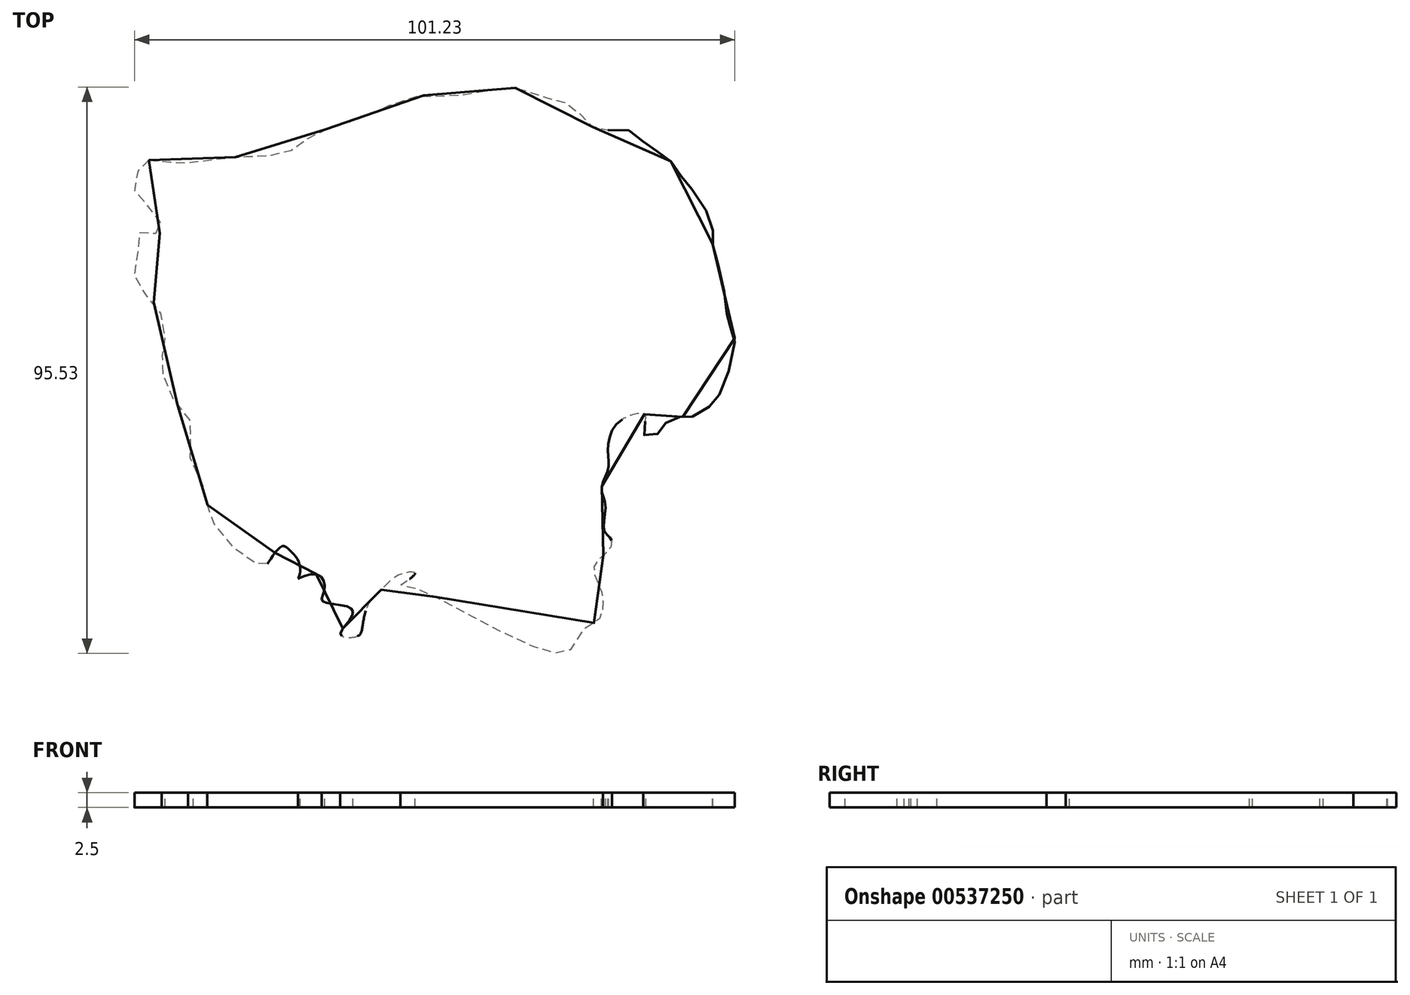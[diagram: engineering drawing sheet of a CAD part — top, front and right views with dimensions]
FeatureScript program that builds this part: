
annotation { "Feature Type Name" : "Feature", "Feature Type Description" : "" }
export const myFeature = defineFeature(function(context is Context, id is Id, definition is map)
    precondition{}
    {
        {
            var Q0;
            Q0=qCreatedBy(makeId("Top.planeOp"),FACE);
            var sketch = newSketch(context, id + "F0", { "sketchPlane" : qUnion([Q0])});
            skFitSpline(sketch, "E0", {"points": [v(-51.17, 29.84) * mm, v(-46.75, 29.42) * mm, v(-44.33, 29.42) * mm, v(-41.03, 29.86) * mm, v(-36.85, 30.3) * mm, v(-33.11, 30.52) * mm, v(-27.83, 31.17) * mm, v(-24.53, 33.38) * mm, v(-19.91, 35.58) * mm, v(-16.17, 36.68) * mm, v(-12.43, 38.22) * mm, v(-5.83, 40.64) * mm, v(0, 40.64) * mm, v(4.07, 41.3) * mm, v(8.9, 41.96) * mm, v(10.02, 42.18) * mm, v(15.73, 40.42) * mm, v(19.03, 39.54) * mm, v(21.9, 37.34) * mm, v(23.21, 35.8) * mm, v(25.41, 34.91) * mm, v(30.25, 34.7) * mm, v(32.9, 32.28) * mm, v(35.98, 30.52) * mm, v(38.4, 27.44) * mm, v(40.38, 25.01) * mm, v(43.9, 18.86) * mm, v(43.9, 16.21) * mm, v(45, 11.81) * mm, v(46.31, 4.34) * mm, v(46.53, 2.57) * mm, v(47.64, 0) * mm, v(45.44, -8.87) * mm, v(43.68, -11.5) * mm, v(40.16, -13.49) * mm, v(38.4, -13.48) * mm, v(35.97, -14.58) * mm, v(34.66, -16.35) * mm, v(32.45, -16.57) * mm, v(32.45, -14.59) * mm, v(32.46, -13.04) * mm, v(28.05, -14.36) * mm, v(26.3, -19.2) * mm, v(26.3, -22.29) * mm, v(25.2, -25.59) * mm, v(25.85, -28.45) * mm, v(25.63, -32.63) * mm, v(26.74, -33.95) * mm, v(26.74, -35.5) * mm, v(24.75, -37.47) * mm, v(23.87, -39.45) * mm, v(24.97, -42.3) * mm, v(25.42, -44.95) * mm, v(24.76, -47.6) * mm, v(21.9, -49.57) * mm, v(18.6, -53.31) * mm, v(-7.14, -42.09) * mm, v(-8.7, -41.87) * mm, v(-6.26, -39.89) * mm, v(-8.91, -40.1) * mm, v(-12.1, -42.75) * mm, v(-13.97, -44.73) * mm, v(-15.07, -48.47) * mm, v(-15.95, -50.46) * mm, v(-18.82, -50.23) * mm, v(-17.05, -47.37) * mm, v(-17.27, -45.61) * mm, v(-21.9, -44.49) * mm, v(-21.5, -42.45) * mm, v(-22.97, -39.97) * mm, v(-26, -40.74) * mm, v(-25.82, -40.4) * mm, v(-25.86, -37.9) * mm, v(-27.4, -35.94) * mm, v(-28.7, -35.29) * mm, v(-30.92, -37.91) * mm, v(-31.78, -38.55) * mm, v(-36.19, -36.15) * mm, v(-41.25, -29.1) * mm, v(-41.26, -27.14) * mm, v(-44.55, -18.54) * mm, v(-43.68, -15.25) * mm, v(-47.19, -10.19) * mm, v(-48.95, -4.02) * mm, v(-48.52, -1.61) * mm, v(-49.4, 4.55) * mm, v(-53.35, 9.4) * mm, v(-52.91, 14.68) * mm, v(-52.24, 17.96) * mm, v(-49.2, 17.55) * mm, v(-50.28, 21.27) * mm, v(-53.34, 24.14) * mm, v(-52.9, 28.1) * mm, v(-51.17, 29.84) * mm]});
            skSolve(sketch);
        }
        {
            var Q0;
            Q0=makeQuery(id+"F0.imprint","IMPRINT",FACE,{"disambiguationData":[TD([[makeQuery(id+"F0.imprint","IMPRINT",EDGE,{"derivedFrom":sQuery(id+"F0.wireOp",EDGE,"E0")}),-1.0]])]});
            extrude(context, id + "F1", {"entities" : qUnion([Q0]), "endBound" : BoundingType.SYMMETRIC, "depth" : 10 * mm, "offsetDistance" : 25 * mm});
        }
        {
            var Q0;
            Q0=makeQuery(id+"F1.opExtrude","CAP_FACE",FACE,{"disambiguationData":[OSD([sQuery(id+"F0.wireOp",EDGE,"E0")])],"isStart":false});
            var Q1;
            Q1=makeQuery(id+"F1.opExtrude","SWEPT_FACE",FACE,{"disambiguationData":[OSD([sQuery(id+"F0.wireOp",EDGE,"E0")])]});
            shell(context, id + "F2", {"entities" : qUnion([Q0, Q1]), "thickness" : 2.5 * mm});
        }
    });
